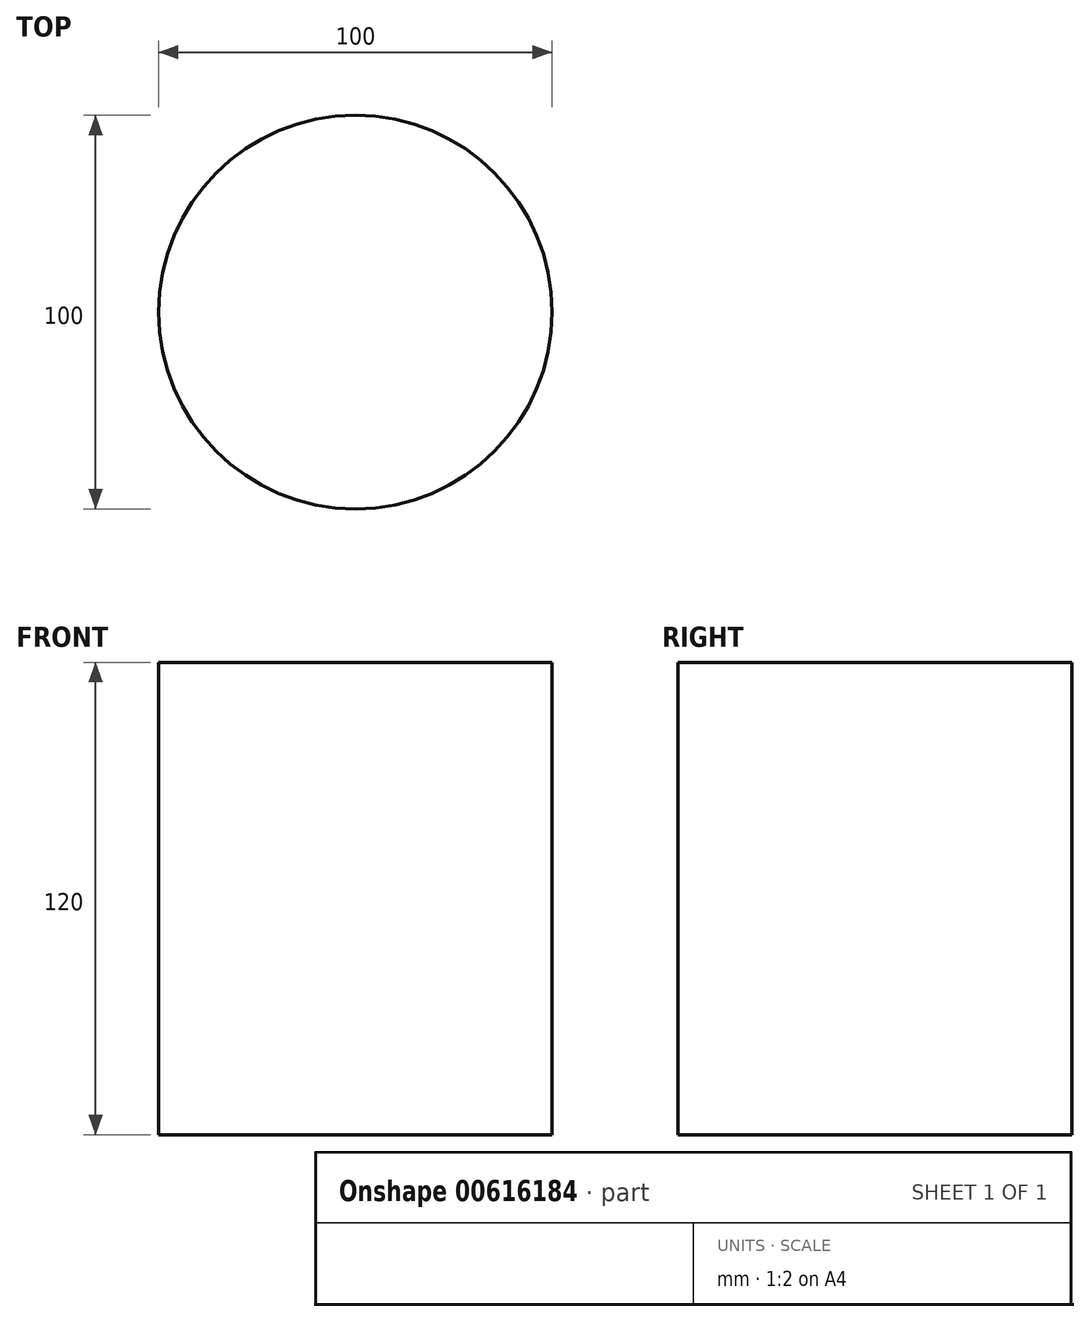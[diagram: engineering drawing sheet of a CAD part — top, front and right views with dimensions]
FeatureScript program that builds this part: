
annotation { "Feature Type Name" : "Feature", "Feature Type Description" : "" }
export const myFeature = defineFeature(function(context is Context, id is Id, definition is map)
    precondition{}
    {
        {
            var Q0;
            Q0=qCreatedBy(makeId("Top.planeOp"),FACE);
            var sketch = newSketch(context, id + "F0", { "sketchPlane" : qUnion([Q0])});
            skCircle(sketch, "E0", {"center": v(0, 0) * mm, "radius": 50 * mm});
            skSolve(sketch);
        }
        {
            var Q0;
            Q0 = qSketchRegion(id + "F0", true);
            extrude(context, id + "F1", {"entities" : qUnion([Q0]), "depth" : 120 * mm, "offsetDistance" : 25 * mm});
        }
    });
